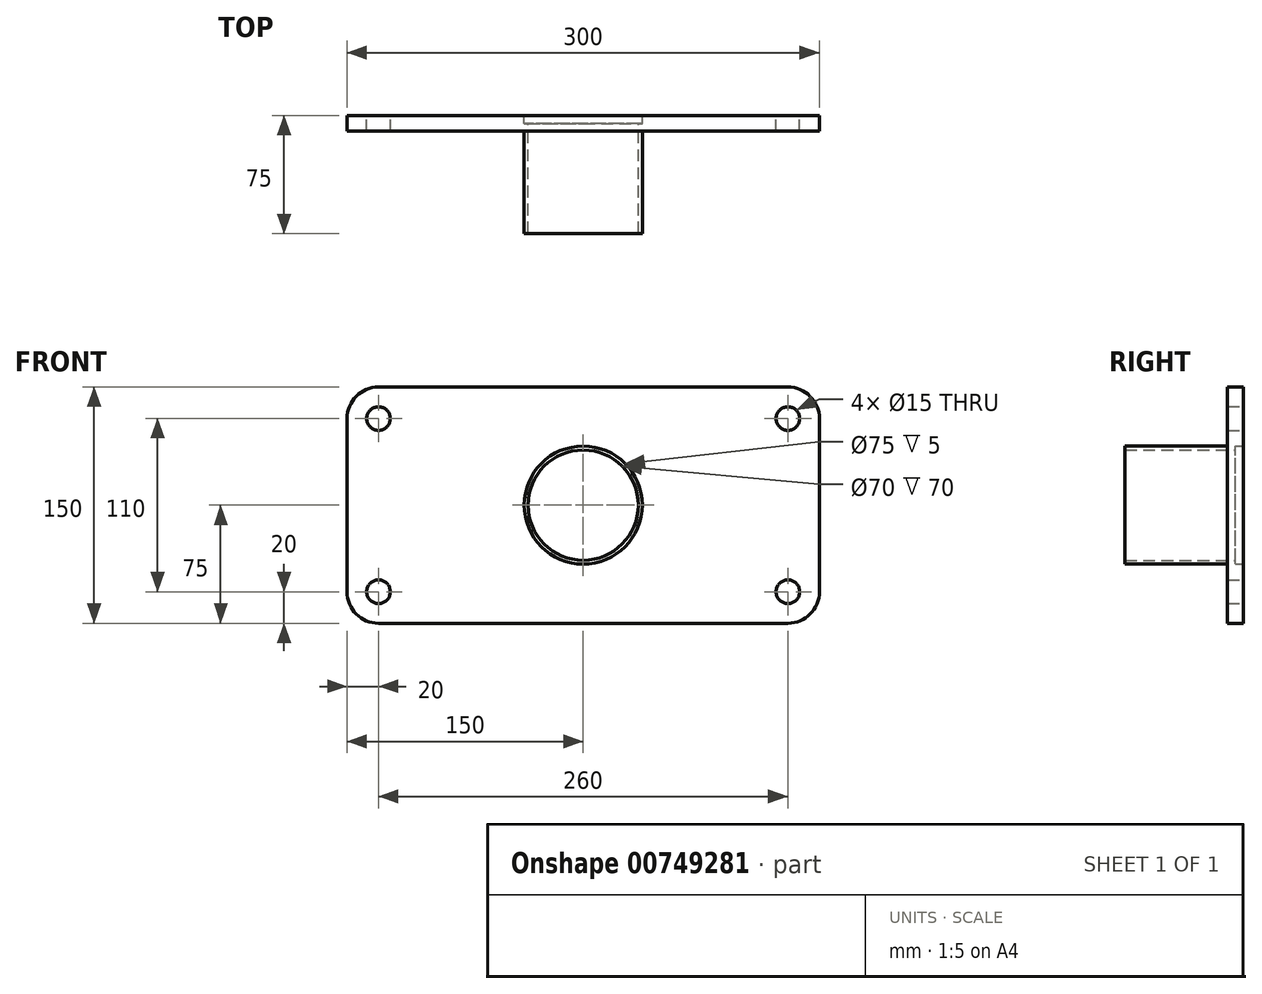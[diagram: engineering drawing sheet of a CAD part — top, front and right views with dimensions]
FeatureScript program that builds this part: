
annotation { "Feature Type Name" : "Feature", "Feature Type Description" : "" }
export const myFeature = defineFeature(function(context is Context, id is Id, definition is map)
    precondition{}
    {
        {
            var Q0;
            Q0=qCreatedBy(makeId("Front.planeOp"),FACE);
            var sketch = newSketch(context, id + "F0", { "sketchPlane" : qUnion([Q0])});
            skLineSegment(sketch, "E0.bottom", {"start": v(130, 75) * mm, "end": v(-130, 75) * mm});
            skLineSegment(sketch, "E0.top", {"start": v(130, -75) * mm, "end": v(-130, -75) * mm});
            skLineSegment(sketch, "E0.left", {"start": v(150, 55) * mm, "end": v(150, -55) * mm});
            skLineSegment(sketch, "E0.right", {"start": v(-150, 55) * mm, "end": v(-150, -55) * mm});
            skPoint(sketch, "E0.middle", {"position": v(0, 0) * mm});
            skPoint(sketch, "E1.visualSharp", {"position": v(-150, 75) * mm});
            skArc(sketch, "E1.filletArc", {"start": v(-130, 75) * mm, "mid": v(-144.14, 69.14) * mm, "end": v(-150, 55) * mm});
            skPoint(sketch, "E2.visualSharp", {"position": v(150, 75) * mm});
            skArc(sketch, "E2.filletArc", {"start": v(150, 55) * mm, "mid": v(144.14, 69.14) * mm, "end": v(130, 75) * mm});
            skPoint(sketch, "E3.visualSharp", {"position": v(150, -75) * mm});
            skArc(sketch, "E3.filletArc", {"start": v(130, -75) * mm, "mid": v(144.14, -69.14) * mm, "end": v(150, -55) * mm});
            skPoint(sketch, "E4.visualSharp", {"position": v(-150, -75) * mm});
            skArc(sketch, "E4.filletArc", {"start": v(-150, -55) * mm, "mid": v(-144.14, -69.14) * mm, "end": v(-130, -75) * mm});
            skCircle(sketch, "E5", {"center": v(-130, 55) * mm, "radius": 7.5 * mm});
            skCircle(sketch, "E6", {"center": v(130, 55) * mm, "radius": 7.5 * mm});
            skCircle(sketch, "E7", {"center": v(130, -55) * mm, "radius": 7.5 * mm});
            skCircle(sketch, "E8", {"center": v(-130, -55) * mm, "radius": 7.5 * mm});
            skCircle(sketch, "E9", {"center": v(0, 0) * mm, "radius": 35 * mm});
            skCircle(sketch, "E10", {"center": v(0, 0) * mm, "radius": 37.5 * mm});
            skSolve(sketch);
        }
        {
            var Q0;
            Q0=makeQuery(id+"F0.imprint","IMPRINT",FACE,{"disambiguationData":[TD([[makeQuery(id+"F0.imprint","IMPRINT",EDGE,{"derivedFrom":sQuery(id+"F0.wireOp",EDGE,"E0.bottom")}),1.0]])]});
            extrude(context, id + "F1", {"entities" : qUnion([Q0]), "depth" : 10 * mm, "offsetDistance" : 25 * mm, "symmetric" : true});
        }
        {
            var Q0;
            Q0=makeQuery(id+"F0.imprint","IMPRINT",FACE,{"disambiguationData":[TD([[makeQuery(id+"F0.imprint","IMPRINT",EDGE,{"derivedFrom":sQuery(id+"F0.wireOp",EDGE,"E9")}),-1.0]])]});
            extrude(context, id + "F2", {"entities" : qUnion([Q0]), "operationType" : NewBodyOperationType.ADD, "depth" : 70 * mm, "offsetDistance" : 25 * mm});
        }
    });
